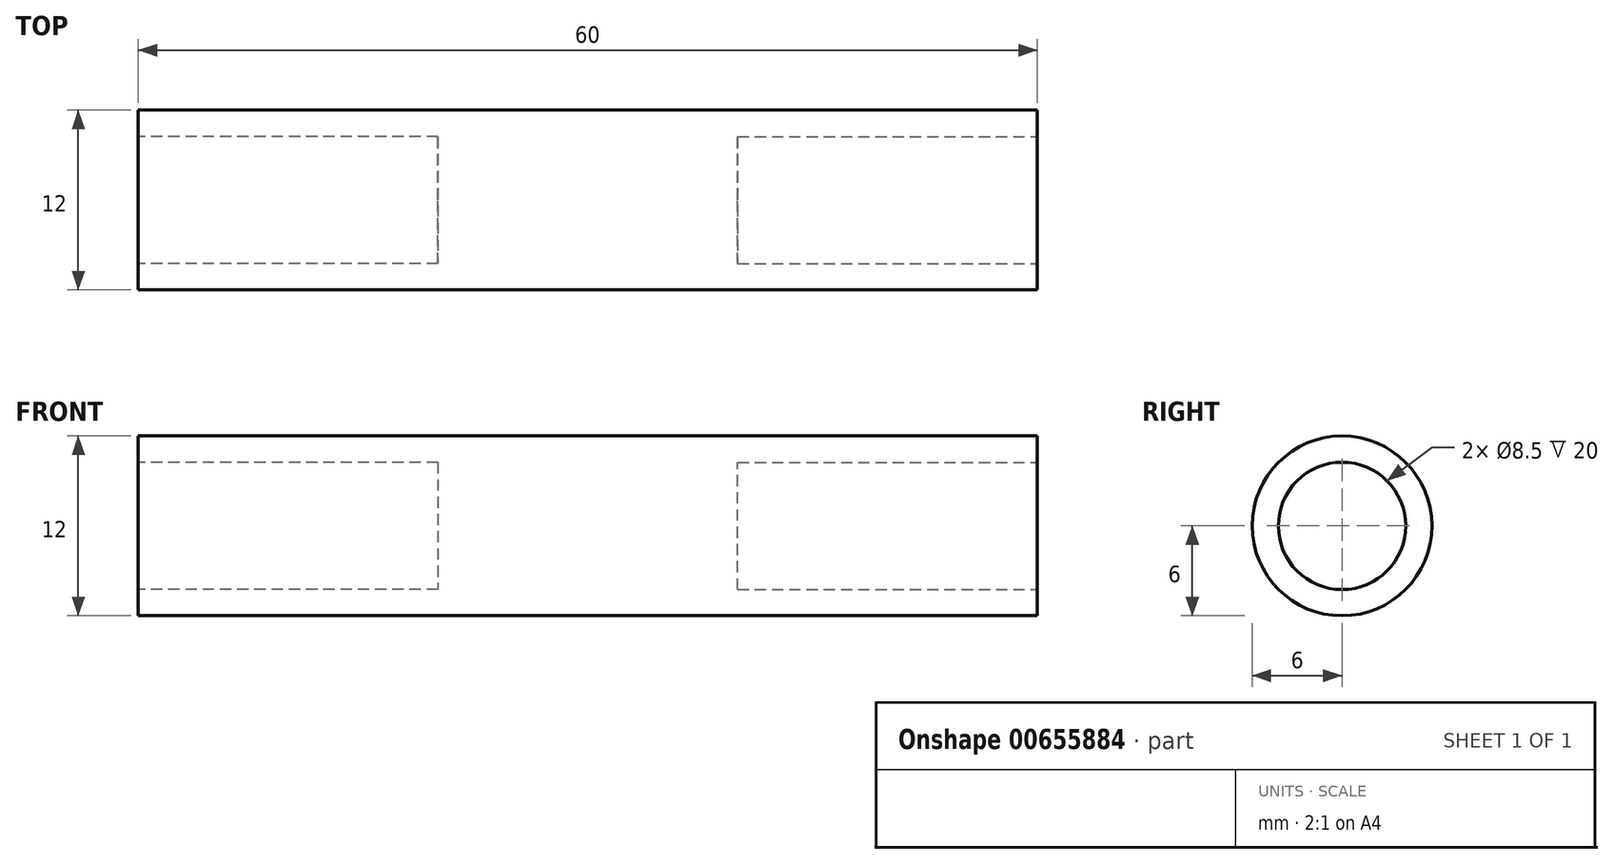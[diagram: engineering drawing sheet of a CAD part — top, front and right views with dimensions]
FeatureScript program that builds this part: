
annotation { "Feature Type Name" : "Feature", "Feature Type Description" : "" }
export const myFeature = defineFeature(function(context is Context, id is Id, definition is map)
    precondition{}
    {
        {
            var Q0;
            Q0=qCreatedBy(makeId("Top.planeOp"),FACE);
            var sketch = newSketch(context, id + "F0", { "sketchPlane" : qUnion([Q0])});
            skLineSegment(sketch, "E0.bottom", {"start": v(30, -6) * mm, "end": v(-30, -6) * mm});
            skLineSegment(sketch, "E0.top", {"start": v(30, 6) * mm, "end": v(-30, 6) * mm});
            skLineSegment(sketch, "E0.left", {"start": v(30, -6) * mm, "end": v(30, 6) * mm});
            skLineSegment(sketch, "E0.right", {"start": v(-30, -6) * mm, "end": v(-30, 6) * mm});
            skPoint(sketch, "E0.middle", {"position": v(0, 0) * mm});
            skSolve(sketch);
        }
        {
            var Q0;
            Q0=makeQuery(id+"F0.imprint","IMPRINT",FACE,{"disambiguationData":[TD([[makeQuery(id+"F0.imprint","IMPRINT",EDGE,{"derivedFrom":sQuery(id+"F0.wireOp",EDGE,"E0.bottom")}),-1.0]])]});
            extrude(context, id + "F1", {"entities" : qUnion([Q0]), "depth" : 12 * mm, "offsetDistance" : 25 * mm});
        }
        {
            var Q0;
            Q0=makeQuery(id+"F1.opExtrude","SWEPT_FACE",FACE,{"disambiguationData":[OSD([sQuery(id+"F0.wireOp",EDGE,"E0.left")])]});
            var sketch = newSketch(context, id + "F2", { "sketchPlane" : qUnion([Q0])});
            skCircle(sketch, "E1", {"center": v(0, 6) * mm, "radius": 4.25 * mm});
            skPoint(sketch, "E1.centerSnap0", {"position": v(6, 6) * mm});
            skSolve(sketch);
        }
        {
            var Q0;
            Q0=makeQuery(id+"F1.opExtrude","SWEPT_FACE",FACE,{"disambiguationData":[OSD([sQuery(id+"F0.wireOp",EDGE,"E0.right")])]});
            var sketch = newSketch(context, id + "F3", { "sketchPlane" : qUnion([Q0])});
            skCircle(sketch, "E2", {"center": v(0, 6) * mm, "radius": 4.25 * mm});
            skPoint(sketch, "E2.centerSnap0", {"position": v(6, 6) * mm});
            skSolve(sketch);
        }
        {
            var Q0;
            Q0=makeQuery(id+"F2.imprint","IMPRINT",FACE,{"disambiguationData":[TD([[makeQuery(id+"F2.imprint","IMPRINT",EDGE,{"derivedFrom":sQuery(id+"F2.wireOp",EDGE,"E1")}),1.0]])]});
            extrude(context, id + "F4", {"entities" : qUnion([Q0]), "operationType" : NewBodyOperationType.REMOVE, "oppositeDirection" : true, "depth" : 20 * mm, "offsetDistance" : 25 * mm});
        }
        {
            var Q0;
            Q0=makeQuery(id+"F3.imprint","IMPRINT",FACE,{"disambiguationData":[TD([[makeQuery(id+"F3.imprint","IMPRINT",EDGE,{"derivedFrom":sQuery(id+"F3.wireOp",EDGE,"E2")}),1.0]])]});
            extrude(context, id + "F5", {"entities" : qUnion([Q0]), "operationType" : NewBodyOperationType.REMOVE, "oppositeDirection" : true, "depth" : 20 * mm, "offsetDistance" : 25 * mm});
        }
        {
            var Q0;
            Q0=makeQuery(id+"F1.opExtrude","CAP_EDGE",EDGE,{"disambiguationData":[OSD([sQuery(id+"F0.wireOp",EDGE,"E0.bottom")])],"isStart":false});
            var Q1;
            Q1=makeQuery(id+"F1.opExtrude","CAP_EDGE",EDGE,{"disambiguationData":[OSD([sQuery(id+"F0.wireOp",EDGE,"E0.bottom")])],"isStart":true});
            var Q2;
            Q2=makeQuery(id+"F1.opExtrude","CAP_EDGE",EDGE,{"disambiguationData":[OSD([sQuery(id+"F0.wireOp",EDGE,"E0.top")])],"isStart":true});
            var Q3;
            Q3=makeQuery(id+"F1.opExtrude","CAP_EDGE",EDGE,{"disambiguationData":[OSD([sQuery(id+"F0.wireOp",EDGE,"E0.top")])],"isStart":false});
            fillet(context, id + "F6", {"entities" : qUnion([Q0, Q1, Q2, Q3]), "radius" : 6 * mm, "tangentPropagation" : true, "allowEdgeOverflow" : false});
        }
    });
